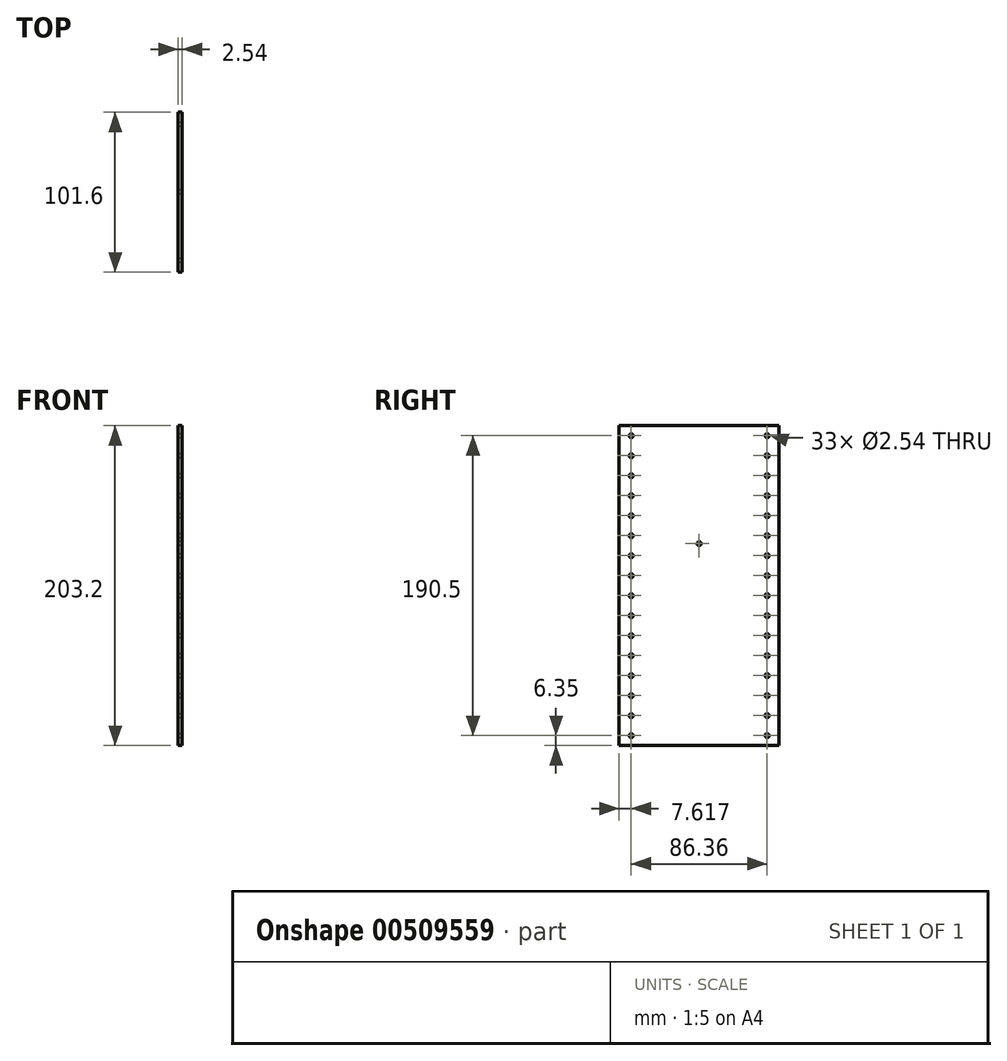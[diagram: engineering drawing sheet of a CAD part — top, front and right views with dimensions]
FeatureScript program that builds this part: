
annotation { "Feature Type Name" : "Feature", "Feature Type Description" : "" }
export const myFeature = defineFeature(function(context is Context, id is Id, definition is map)
    precondition{}
    {
        {
            var Q0;
            Q0=qCreatedBy(makeId("Right.planeOp"),FACE);
            var sketch = newSketch(context, id + "F0", { "sketchPlane" : qUnion([Q0])});
            skLineSegment(sketch, "E0.bottom", {"start": v(-109.98, 0) * mm, "end": v(-211.58, 0) * mm});
            skLineSegment(sketch, "E0.top", {"start": v(-109.98, 203.2) * mm, "end": v(-211.58, 203.2) * mm});
            skLineSegment(sketch, "E0.left", {"start": v(-109.98, 0) * mm, "end": v(-109.98, 203.2) * mm});
            skLineSegment(sketch, "E0.right", {"start": v(-211.58, 0) * mm, "end": v(-211.58, 203.2) * mm});
            skSolve(sketch);
        }
        {
            var Q0;
            Q0=makeQuery(id+"F0.imprint","IMPRINT",FACE,{"disambiguationData":[TD([[makeQuery(id+"F0.imprint","IMPRINT",EDGE,{"derivedFrom":sQuery(id+"F0.wireOp",EDGE,"E0.bottom")}),-1.0]])]});
            extrude(context, id + "F1", {"entities" : qUnion([Q0]), "depth" : 2.54 * mm});
        }
        {
            var Q0;
            Q0=makeQuery(id+"F1.opExtrude","CAP_FACE",FACE,{"disambiguationData":[OSD([sQuery(id+"F0.wireOp",EDGE,"E0.bottom"),sQuery(id+"F0.wireOp",EDGE,"E0.top"),sQuery(id+"F0.wireOp",EDGE,"E0.left"),sQuery(id+"F0.wireOp",EDGE,"E0.right")])],"isStart":false});
            var sketch = newSketch(context, id + "F2", { "sketchPlane" : qUnion([Q0])});
            skLineSegment(sketch, "E1", {"start": v(-211.58, 0) * mm, "end": v(-203.96, 0) * mm});
            skLineSegment(sketch, "E2", {"start": v(-203.96, 0) * mm, "end": v(-203.96, 6.35) * mm});
            skCircle(sketch, "E3", {"center": v(-203.96, 6.35) * mm, "radius": 1.27 * mm});
            skCircle(sketch, "E4.0.1.0", {"center": v(-203.96, 19.05) * mm, "radius": 1.27 * mm});
            skCircle(sketch, "E4.0.2.0", {"center": v(-203.96, 31.75) * mm, "radius": 1.27 * mm});
            skCircle(sketch, "E4.0.3.0", {"center": v(-203.96, 44.45) * mm, "radius": 1.27 * mm});
            skCircle(sketch, "E4.0.4.0", {"center": v(-203.96, 57.15) * mm, "radius": 1.27 * mm});
            skCircle(sketch, "E4.0.5.0", {"center": v(-203.96, 69.85) * mm, "radius": 1.27 * mm});
            skCircle(sketch, "E4.0.6.0", {"center": v(-203.96, 82.55) * mm, "radius": 1.27 * mm});
            skCircle(sketch, "E4.0.7.0", {"center": v(-203.96, 95.25) * mm, "radius": 1.27 * mm});
            skCircle(sketch, "E4.0.8.0", {"center": v(-203.96, 107.95) * mm, "radius": 1.27 * mm});
            skCircle(sketch, "E4.0.9.0", {"center": v(-203.96, 120.65) * mm, "radius": 1.27 * mm});
            skCircle(sketch, "E4.0.10.0", {"center": v(-203.96, 133.35) * mm, "radius": 1.27 * mm});
            skCircle(sketch, "E4.0.11.0", {"center": v(-203.96, 146.05) * mm, "radius": 1.27 * mm});
            skCircle(sketch, "E4.0.12.0", {"center": v(-203.96, 158.75) * mm, "radius": 1.27 * mm});
            skCircle(sketch, "E4.0.13.0", {"center": v(-203.96, 171.45) * mm, "radius": 1.27 * mm});
            skCircle(sketch, "E4.0.14.0", {"center": v(-203.96, 184.15) * mm, "radius": 1.27 * mm});
            skCircle(sketch, "E4.0.15.0", {"center": v(-203.96, 196.85) * mm, "radius": 1.27 * mm});
            skCircle(sketch, "E4.1.0.0", {"center": v(-117.6, 6.35) * mm, "radius": 1.27 * mm});
            skCircle(sketch, "E4.1.1.0", {"center": v(-117.6, 19.05) * mm, "radius": 1.27 * mm});
            skCircle(sketch, "E4.1.2.0", {"center": v(-117.6, 31.75) * mm, "radius": 1.27 * mm});
            skCircle(sketch, "E4.1.3.0", {"center": v(-117.6, 44.45) * mm, "radius": 1.27 * mm});
            skCircle(sketch, "E4.1.4.0", {"center": v(-117.6, 57.15) * mm, "radius": 1.27 * mm});
            skCircle(sketch, "E4.1.5.0", {"center": v(-117.6, 69.85) * mm, "radius": 1.27 * mm});
            skCircle(sketch, "E4.1.6.0", {"center": v(-117.6, 82.55) * mm, "radius": 1.27 * mm});
            skCircle(sketch, "E4.1.7.0", {"center": v(-117.6, 95.25) * mm, "radius": 1.27 * mm});
            skCircle(sketch, "E4.1.8.0", {"center": v(-117.6, 107.95) * mm, "radius": 1.27 * mm});
            skCircle(sketch, "E4.1.9.0", {"center": v(-117.6, 120.65) * mm, "radius": 1.27 * mm});
            skCircle(sketch, "E4.1.10.0", {"center": v(-117.6, 133.35) * mm, "radius": 1.27 * mm});
            skCircle(sketch, "E4.1.11.0", {"center": v(-117.6, 146.05) * mm, "radius": 1.27 * mm});
            skCircle(sketch, "E4.1.12.0", {"center": v(-117.6, 158.75) * mm, "radius": 1.27 * mm});
            skCircle(sketch, "E4.1.13.0", {"center": v(-117.6, 171.45) * mm, "radius": 1.27 * mm});
            skCircle(sketch, "E4.1.14.0", {"center": v(-117.6, 184.15) * mm, "radius": 1.27 * mm});
            skCircle(sketch, "E4.1.15.0", {"center": v(-117.6, 196.85) * mm, "radius": 1.27 * mm});
            skLineSegment(sketch, "E4.direction1", {"start": v(-203.96, 6.35) * mm, "end": v(-117.6, 6.35) * mm, "construction": true});
            skLineSegment(sketch, "E4.direction2", {"start": v(-203.96, 6.35) * mm, "end": v(-203.96, 19.05) * mm, "construction": true});
            skSolve(sketch);
        }
        {
            var Q0;
            Q0=makeQuery(id+"F2.imprint","IMPRINT",FACE,{"disambiguationData":[TD([[makeQuery(id+"F2.imprint","IMPRINT",EDGE,{"derivedFrom":sQuery(id+"F2.wireOp",EDGE,"E4.0.8.0")}),1.0]])]});
            var Q1;
            Q1=makeQuery(id+"F2.imprint","IMPRINT",FACE,{"disambiguationData":[TD([[makeQuery(id+"F2.imprint","IMPRINT",EDGE,{"derivedFrom":sQuery(id+"F2.wireOp",EDGE,"E4.0.9.0")}),1.0]])]});
            var Q2;
            Q2=makeQuery(id+"F2.imprint","IMPRINT",FACE,{"disambiguationData":[TD([[makeQuery(id+"F2.imprint","IMPRINT",EDGE,{"derivedFrom":sQuery(id+"F2.wireOp",EDGE,"E4.0.10.0")}),1.0]])]});
            var Q3;
            Q3=makeQuery(id+"F2.imprint","IMPRINT",FACE,{"disambiguationData":[TD([[makeQuery(id+"F2.imprint","IMPRINT",EDGE,{"derivedFrom":sQuery(id+"F2.wireOp",EDGE,"E4.0.11.0")}),1.0]])]});
            var Q4;
            Q4=makeQuery(id+"F2.imprint","IMPRINT",FACE,{"disambiguationData":[TD([[makeQuery(id+"F2.imprint","IMPRINT",EDGE,{"derivedFrom":sQuery(id+"F2.wireOp",EDGE,"E4.1.9.0")}),1.0]])]});
            var Q5;
            Q5=makeQuery(id+"F2.imprint","IMPRINT",FACE,{"disambiguationData":[TD([[makeQuery(id+"F2.imprint","IMPRINT",EDGE,{"derivedFrom":sQuery(id+"F2.wireOp",EDGE,"E4.1.11.0")}),1.0]])]});
            var Q6;
            Q6=makeQuery(id+"F2.imprint","IMPRINT",FACE,{"disambiguationData":[TD([[makeQuery(id+"F2.imprint","IMPRINT",EDGE,{"derivedFrom":sQuery(id+"F2.wireOp",EDGE,"E4.1.7.0")}),1.0]])]});
            var Q7;
            Q7=makeQuery(id+"F2.imprint","IMPRINT",FACE,{"disambiguationData":[TD([[makeQuery(id+"F2.imprint","IMPRINT",EDGE,{"derivedFrom":sQuery(id+"F2.wireOp",EDGE,"E4.1.14.0")}),1.0]])]});
            var Q8;
            Q8=makeQuery(id+"F2.imprint","IMPRINT",FACE,{"disambiguationData":[TD([[makeQuery(id+"F2.imprint","IMPRINT",EDGE,{"derivedFrom":sQuery(id+"F2.wireOp",EDGE,"E4.1.5.0")}),1.0]])]});
            var Q9;
            Q9=makeQuery(id+"F2.imprint","IMPRINT",FACE,{"disambiguationData":[TD([[makeQuery(id+"F2.imprint","IMPRINT",EDGE,{"derivedFrom":sQuery(id+"F2.wireOp",EDGE,"E4.1.1.0")}),1.0]])]});
            var Q10;
            Q10=makeQuery(id+"F2.imprint","IMPRINT",FACE,{"disambiguationData":[TD([[makeQuery(id+"F2.imprint","IMPRINT",EDGE,{"derivedFrom":sQuery(id+"F2.wireOp",EDGE,"E4.1.12.0")}),1.0]])]});
            var Q11;
            Q11=makeQuery(id+"F2.imprint","IMPRINT",FACE,{"disambiguationData":[TD([[makeQuery(id+"F2.imprint","IMPRINT",EDGE,{"derivedFrom":sQuery(id+"F2.wireOp",EDGE,"E4.1.8.0")}),1.0]])]});
            var Q12;
            Q12=makeQuery(id+"F2.imprint","IMPRINT",FACE,{"disambiguationData":[TD([[makeQuery(id+"F2.imprint","IMPRINT",EDGE,{"derivedFrom":sQuery(id+"F2.wireOp",EDGE,"E4.1.2.0")}),1.0]])]});
            var Q13;
            Q13=makeQuery(id+"F2.imprint","IMPRINT",FACE,{"disambiguationData":[TD([[makeQuery(id+"F2.imprint","IMPRINT",EDGE,{"derivedFrom":sQuery(id+"F2.wireOp",EDGE,"E4.0.15.0")}),1.0]])]});
            var Q14;
            Q14=makeQuery(id+"F2.imprint","IMPRINT",FACE,{"disambiguationData":[TD([[makeQuery(id+"F2.imprint","IMPRINT",EDGE,{"derivedFrom":sQuery(id+"F2.wireOp",EDGE,"E4.0.13.0")}),1.0]])]});
            var Q15;
            Q15=makeQuery(id+"F2.imprint","IMPRINT",FACE,{"disambiguationData":[TD([[makeQuery(id+"F2.imprint","IMPRINT",EDGE,{"derivedFrom":sQuery(id+"F2.wireOp",EDGE,"E4.0.14.0")}),1.0]])]});
            var Q16;
            Q16=makeQuery(id+"F2.imprint","IMPRINT",FACE,{"disambiguationData":[TD([[makeQuery(id+"F2.imprint","IMPRINT",EDGE,{"derivedFrom":sQuery(id+"F2.wireOp",EDGE,"E4.0.1.0")}),1.0]])]});
            var Q17;
            Q17=makeQuery(id+"F2.imprint","IMPRINT",FACE,{"disambiguationData":[TD([[makeQuery(id+"F2.imprint","IMPRINT",EDGE,{"derivedFrom":sQuery(id+"F2.wireOp",EDGE,"E4.0.2.0")}),1.0]])]});
            var Q18;
            Q18=makeQuery(id+"F2.imprint","IMPRINT",FACE,{"disambiguationData":[TD([[makeQuery(id+"F2.imprint","IMPRINT",EDGE,{"derivedFrom":sQuery(id+"F2.wireOp",EDGE,"E4.0.3.0")}),1.0]])]});
            var Q19;
            Q19=makeQuery(id+"F2.imprint","IMPRINT",FACE,{"disambiguationData":[TD([[makeQuery(id+"F2.imprint","IMPRINT",EDGE,{"derivedFrom":sQuery(id+"F2.wireOp",EDGE,"E4.0.4.0")}),1.0]])]});
            var Q20;
            Q20=makeQuery(id+"F2.imprint","IMPRINT",FACE,{"disambiguationData":[TD([[makeQuery(id+"F2.imprint","IMPRINT",EDGE,{"derivedFrom":sQuery(id+"F2.wireOp",EDGE,"E4.0.5.0")}),1.0]])]});
            var Q21;
            Q21=makeQuery(id+"F2.imprint","IMPRINT",FACE,{"disambiguationData":[TD([[makeQuery(id+"F2.imprint","IMPRINT",EDGE,{"derivedFrom":sQuery(id+"F2.wireOp",EDGE,"E4.0.6.0")}),1.0]])]});
            var Q22;
            Q22=makeQuery(id+"F2.imprint","IMPRINT",FACE,{"disambiguationData":[TD([[makeQuery(id+"F2.imprint","IMPRINT",EDGE,{"derivedFrom":sQuery(id+"F2.wireOp",EDGE,"E4.0.7.0")}),1.0]])]});
            var Q23;
            Q23=makeQuery(id+"F2.imprint","IMPRINT",FACE,{"disambiguationData":[TD([[makeQuery(id+"F2.imprint","IMPRINT",EDGE,{"derivedFrom":sQuery(id+"F2.wireOp",EDGE,"E4.1.15.0")}),1.0]])]});
            var Q24;
            Q24=makeQuery(id+"F2.imprint","IMPRINT",FACE,{"disambiguationData":[TD([[makeQuery(id+"F2.imprint","IMPRINT",EDGE,{"derivedFrom":sQuery(id+"F2.wireOp",EDGE,"E4.0.12.0")}),1.0]])]});
            var Q25;
            Q25=makeQuery(id+"F2.imprint","IMPRINT",FACE,{"disambiguationData":[TD([[makeQuery(id+"F2.imprint","IMPRINT",EDGE,{"derivedFrom":sQuery(id+"F2.wireOp",EDGE,"E4.1.3.0")}),1.0]])]});
            var Q26;
            Q26=makeQuery(id+"F2.imprint","IMPRINT",FACE,{"disambiguationData":[TD([[makeQuery(id+"F2.imprint","IMPRINT",EDGE,{"derivedFrom":sQuery(id+"F2.wireOp",EDGE,"E4.1.6.0")}),1.0]])]});
            var Q27;
            Q27=makeQuery(id+"F2.imprint","IMPRINT",FACE,{"disambiguationData":[TD([[makeQuery(id+"F2.imprint","IMPRINT",EDGE,{"derivedFrom":sQuery(id+"F2.wireOp",EDGE,"E4.1.10.0")}),1.0]])]});
            var Q28;
            Q28=makeQuery(id+"F2.imprint","IMPRINT",FACE,{"disambiguationData":[TD([[makeQuery(id+"F2.imprint","IMPRINT",EDGE,{"derivedFrom":sQuery(id+"F2.wireOp",EDGE,"E4.1.13.0")}),1.0]])]});
            var Q29;
            Q29=makeQuery(id+"F2.imprint","IMPRINT",FACE,{"disambiguationData":[TD([[makeQuery(id+"F2.imprint","IMPRINT",EDGE,{"derivedFrom":sQuery(id+"F2.wireOp",EDGE,"E4.1.4.0")}),1.0]])]});
            var Q30;
            Q30=makeQuery(id+"F2.imprint","IMPRINT",FACE,{"disambiguationData":[TD([[makeQuery(id+"F2.imprint","IMPRINT",EDGE,{"derivedFrom":sQuery(id+"F2.wireOp",EDGE,"E4.1.0.0")}),1.0]])]});
            var Q31;
            Q31=makeQuery(id+"F2.imprint","IMPRINT",FACE,{"disambiguationData":[TD([[makeQuery(id+"F2.imprint","IMPRINT",EDGE,{"derivedFrom":sQuery(id+"F2.wireOp",EDGE,"E3")}),1.0]])]});
            extrude(context, id + "F3", {"entities" : qUnion([Q0, Q1, Q2, Q3, Q4, Q5, Q6, Q7, Q8, Q9, Q10, Q11, Q12, Q13, Q14, Q15, Q16, Q17, Q18, Q19, Q20, Q21, Q22, Q23, Q24, Q25, Q26, Q27, Q28, Q29, Q30, Q31]), "operationType" : NewBodyOperationType.REMOVE, "oppositeDirection" : true, "depth" : 25.4 * mm});
        }
        {
            var Q0;
            Q0=makeQuery(id+"F1.opExtrude","CAP_FACE",FACE,{"disambiguationData":[OSD([sQuery(id+"F0.wireOp",EDGE,"E0.bottom"),sQuery(id+"F0.wireOp",EDGE,"E0.top"),sQuery(id+"F0.wireOp",EDGE,"E0.left"),sQuery(id+"F0.wireOp",EDGE,"E0.right")])],"isStart":true});
            var sketch = newSketch(context, id + "F4", { "sketchPlane" : qUnion([Q0])});
            skCircle(sketch, "E5", {"center": v(160.81, 128.27) * mm, "radius": 1.27 * mm});
            skSolve(sketch);
        }
        {
            var Q0;
            Q0=makeQuery(id+"F4.imprint","IMPRINT",FACE,{"disambiguationData":[TD([[makeQuery(id+"F4.imprint","IMPRINT",EDGE,{"derivedFrom":sQuery(id+"F4.wireOp",EDGE,"E5")}),1.0]])]});
            extrude(context, id + "F5", {"entities" : qUnion([Q0]), "operationType" : NewBodyOperationType.REMOVE, "oppositeDirection" : true, "depth" : 25.4 * mm});
        }
    });
